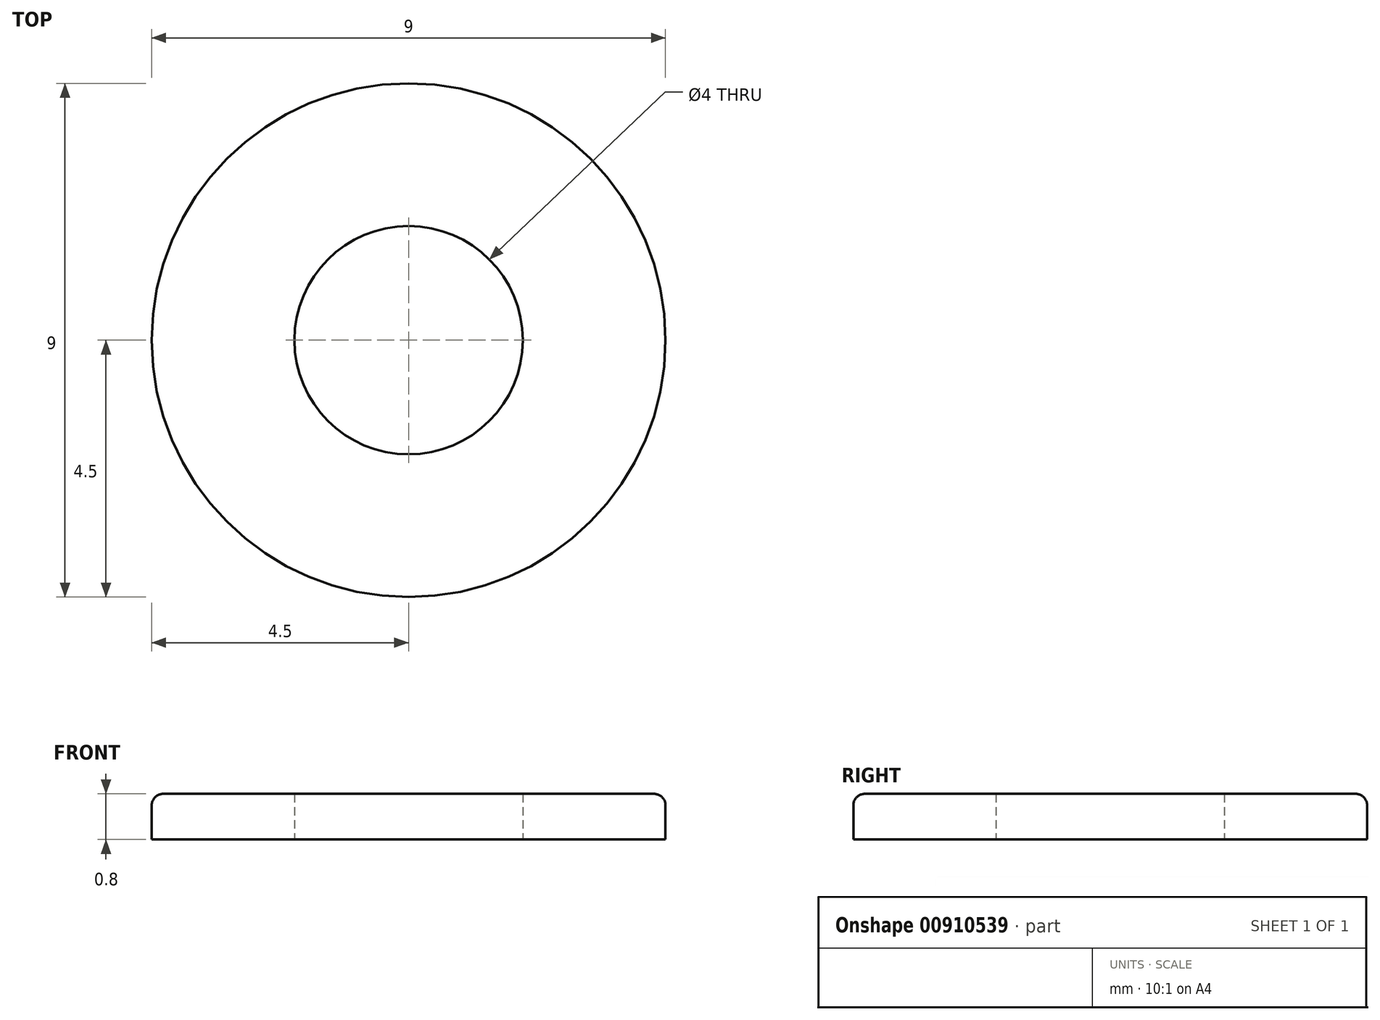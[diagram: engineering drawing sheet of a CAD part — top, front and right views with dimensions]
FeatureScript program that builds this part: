
annotation { "Feature Type Name" : "Feature", "Feature Type Description" : "" }
export const myFeature = defineFeature(function(context is Context, id is Id, definition is map)
    precondition{}
    {
        {
            var Q0;
            Q0=qCreatedBy(makeId("Top.planeOp"),FACE);
            var sketch = newSketch(context, id + "F0", { "sketchPlane" : qUnion([Q0])});
            skCircle(sketch, "E0", {"center": v(0, 0) * mm, "radius": 4.5 * mm});
            skCircle(sketch, "E1", {"center": v(0, 0) * mm, "radius": 2 * mm});
            skSolve(sketch);
        }
        {
            var Q0;
            Q0 = qSketchRegion(id + "F0", true);
            extrude(context, id + "F1", {"entities" : qUnion([Q0]), "depth" : .8 * mm, "offsetDistance" : 25 * mm});
        }
        {
            var Q0;
            Q0=makeQuery(id+"F1.opExtrude","CAP_EDGE",EDGE,{"disambiguationData":[OSD([sQuery(id+"F0.wireOp",EDGE,"E0")])],"isStart":false});
            fillet(context, id + "F2", {"entities" : qUnion([Q0]), "radius" : .2 * mm, "tangentPropagation" : true, "allowEdgeOverflow" : false});
        }
    });
